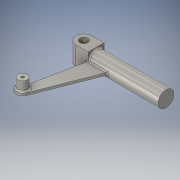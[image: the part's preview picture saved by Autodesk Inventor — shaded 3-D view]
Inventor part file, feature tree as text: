
AUTODESK INVENTOR PART (.ipt)
format: ipt  version: 2016 (Build 200138000, 138)  size: 226,304 bytes
history: native  units: in
note: dims shown in document units (in); Inventor stores cm internally (conversion verified against a paired STEP export)
features: other x6, extrude x5, sketch x5, fillet x2, hole x1
ambient origin geometry x8: Origin, YZ Plane, XZ Plane, XY Plane, X Axis, Y Axis, Z Axis, Center Point
bodies: Solid1 (feature_tree)
feature tree (19):
  extrude  "Main Plate"  Depth=0.5in
  other  "Axle Centerline"
  extrude  "Tie Rod Standoff"  Depth=5.0in
  hole  "Tie Rod Hole"  [1 undecoded]
  fillet  "Weld1"  Radius=0.125in
  extrude  "Main Plate Fix"  Depth=0.75in
  other  "Axle Hole Plane"
  extrude  "Axle Cylinder"  Depth=0.125in
  other  "Main Plate Midplane1"
  extrude  "Rotational Hole"  Depth=0.125in
  other  "Rotational Hole Axis"
  fillet  "Weld2"  Radius=0.1in
  other  "Work Point1"
  sketch  "Sketch1"  dims[d0=1.0in d1=0.5in]
  other  "Main Plate Midplane"
  sketch  "Sketch5"  dims[d2=1.5in d6=5.0in]
  sketch  "Sketch6"  dims[d7=0.625in d8=0.75in d9=0.125in]
  sketch  "Sketch7"  dims[d10=0.1875in d11=0.0in d31=0.75in]
  sketch  "Sketch9"  dims[d32=0.75in d33=0.0in d34=1.0in d35=1.0in d36=0.211in d37=0.5in d38=0.375in d39=0.25in d40=0.5635in d41=0.679in d42=0.8108in d43=0.125in d44=0.1in d45=0.1in d46=0.1875in d47=0.0in d49=0.0in d50=0.1in d51=1.25in d53=5.5in d54=0.0in d55=0.625in d56=0.625in d57=1.5in d58=0.0in d59=0.125in]
note: 1 required parameter value undecoded (feature->parameter linkage not recoverable at this tier; creation-order binding heuristic only, values carry confidence <= 0.55)
